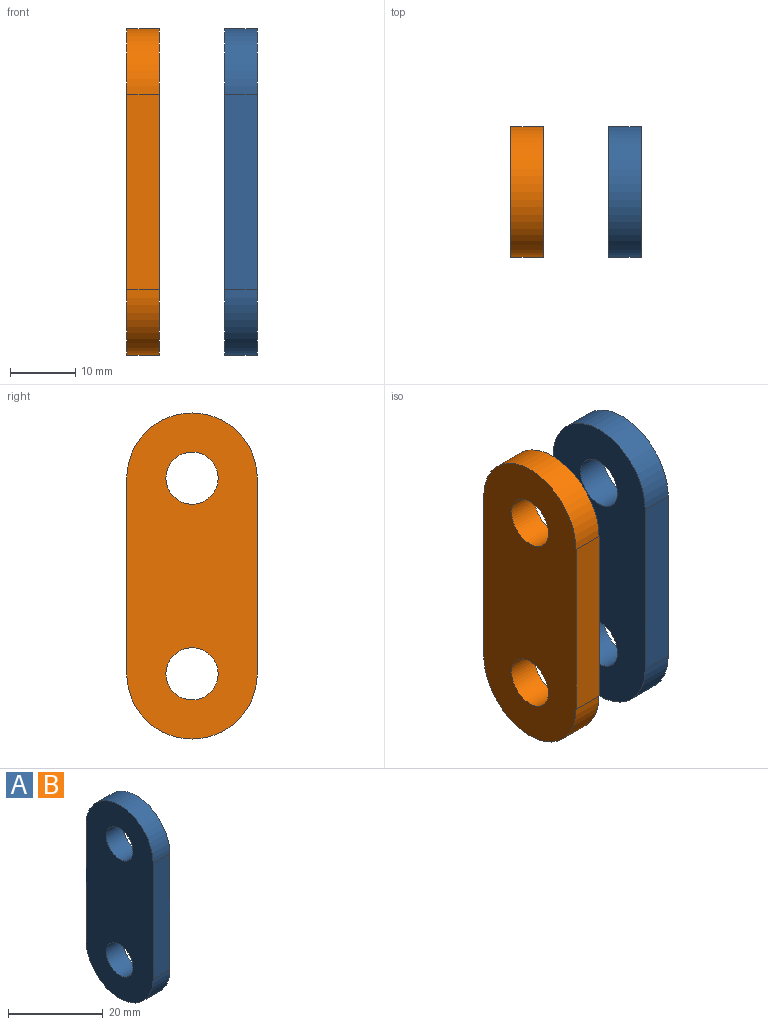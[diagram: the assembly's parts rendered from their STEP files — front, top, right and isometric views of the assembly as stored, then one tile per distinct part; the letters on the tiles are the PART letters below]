
ASSEMBLY  parts=2 mates=1
PART A: 8 faces, bbox 5x20x50 mm
  f0: cylinder r=10mm len=20mm, axis (-1,0,0), area 157.1mm2, adj f1,f5,f6,f7
  f1: plane 30x5mm, normal (0,-1,0), area 150mm2, adj f0,f2,f6,f7
  f2: cylinder r=10mm len=20mm, axis (-1,0,0), area 157.1mm2, adj f1,f5,f6,f7
  f3: cylinder r=4mm len=8mm, axis (-1,0,0), area 125.7mm2, adj f6,f7
  f4: cylinder r=4mm len=8mm, axis (-1,0,0), area 125.7mm2, adj f6,f7
  f5: plane 30x5mm, normal (0,1,0), area 150mm2, adj f0,f2,f6,f7
  f6: plane 50x20mm, normal (1,0,0), area 813.6mm2, adj f0,f1,f2,f3,f4,f5
  f7: plane 50x20mm, normal (-1,0,0), area 813.6mm2, adj f0,f1,f2,f3,f4,f5
PART B: same geometry as A
PLACE A t=(7.5,0,0)mm
PLACE B t=(-7.5,0,0)mm
MATE fastened B.f2 <-> A.f2  axis (-1,0,0) through (-5,0,0)mm
